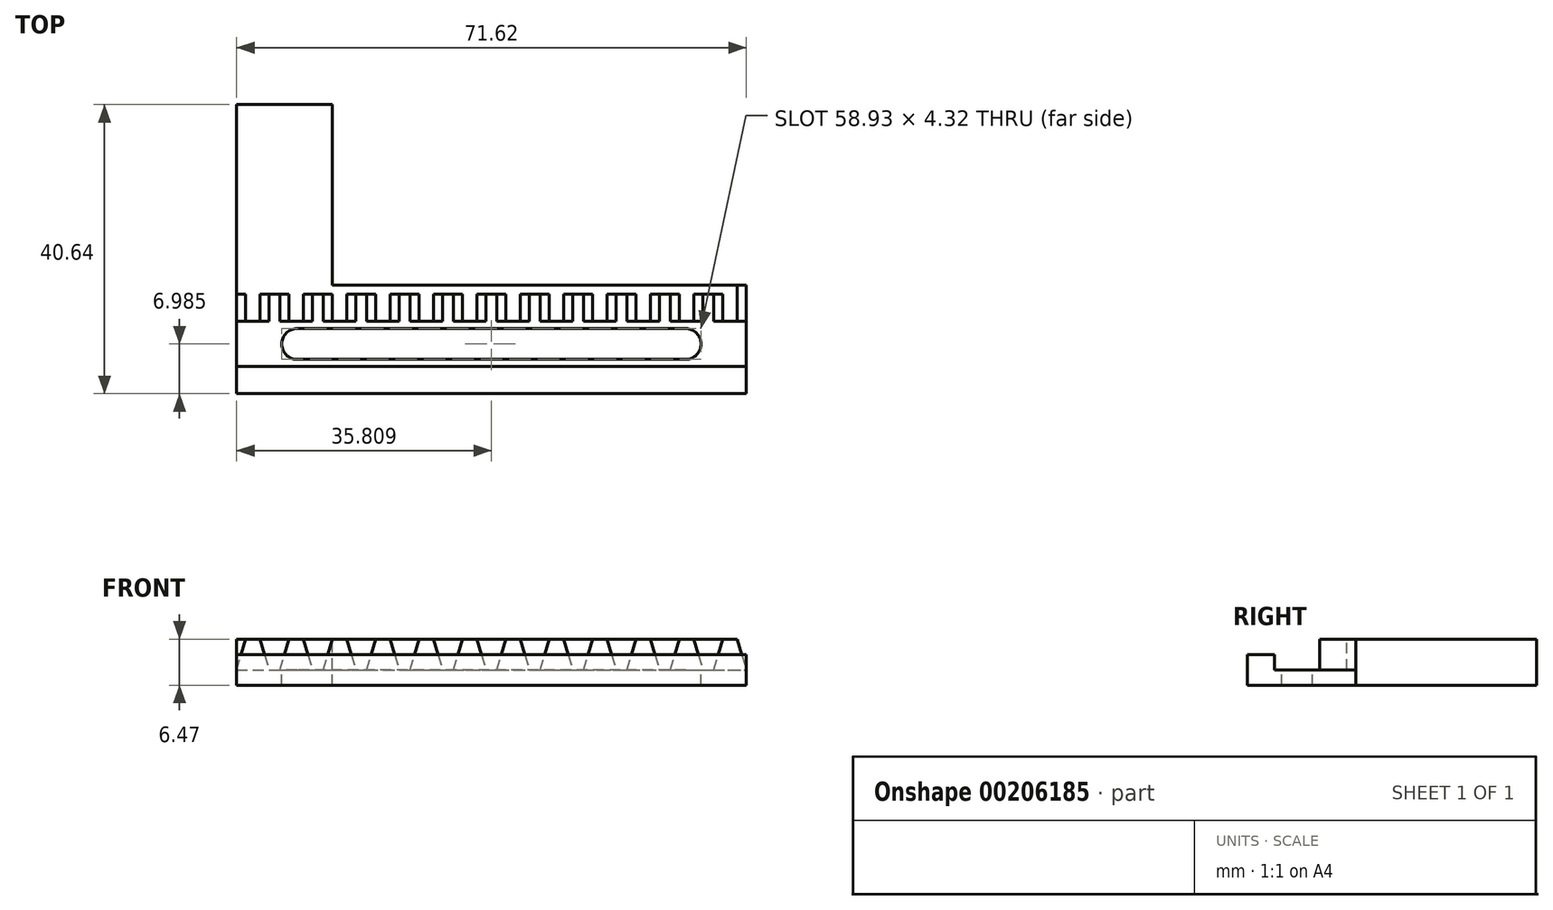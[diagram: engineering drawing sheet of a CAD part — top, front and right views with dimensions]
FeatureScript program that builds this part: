
annotation { "Feature Type Name" : "Feature", "Feature Type Description" : "" }
export const myFeature = defineFeature(function(context is Context, id is Id, definition is map)
    precondition{}
    {
        {
            var Q0;
            Q0=qCreatedBy(makeId("Front.planeOp"),FACE);
            var sketch = newSketch(context, id + "F0", { "sketchPlane" : qUnion([Q0])});
            skLineSegment(sketch, "E0.bottom", {"start": v(-38.44, 14.74) * mm, "end": v(33.18, 14.74) * mm});
            skLineSegment(sketch, "E0.top", {"start": v(-38.44, 16.9) * mm, "end": v(33.18, 16.9) * mm});
            skLineSegment(sketch, "E0.left", {"start": v(-38.44, 14.74) * mm, "end": v(-38.44, 16.9) * mm});
            skLineSegment(sketch, "E1", {"start": v(-38.44, 16.9) * mm, "end": v(-37.17, 21.21) * mm});
            skLineSegment(sketch, "E2", {"start": v(-37.17, 21.21) * mm, "end": v(-35.14, 21.21) * mm});
            skLineSegment(sketch, "E3", {"start": v(-35.14, 21.21) * mm, "end": v(-33.87, 16.9) * mm});
            skLineSegment(sketch, "E4", {"start": v(-38.44, 16.9) * mm, "end": v(-33.87, 16.9) * mm});
            skLineSegment(sketch, "E5", {"start": v(-36.16, 21.21) * mm, "end": v(-36.16, 16.9) * mm, "construction": true});
            skLineSegment(sketch, "E6", {"start": v(33.18, 14.74) * mm, "end": v(33.18, 16.9) * mm});
            skLineSegment(sketch, "E7.1.0.0", {"start": v(-29.05, 21.21) * mm, "end": v(-27.78, 16.9) * mm});
            skLineSegment(sketch, "E7.1.0.1", {"start": v(-32.35, 16.9) * mm, "end": v(-31.08, 21.21) * mm});
            skLineSegment(sketch, "E7.1.0.2", {"start": v(-31.08, 21.21) * mm, "end": v(-29.05, 21.21) * mm});
            skLineSegment(sketch, "E7.2.0.0", {"start": v(-22.95, 21.21) * mm, "end": v(-21.68, 16.9) * mm});
            skLineSegment(sketch, "E7.2.0.1", {"start": v(-26.25, 16.9) * mm, "end": v(-24.98, 21.21) * mm});
            skLineSegment(sketch, "E7.2.0.2", {"start": v(-24.98, 21.21) * mm, "end": v(-22.95, 21.21) * mm});
            skLineSegment(sketch, "E7.3.0.0", {"start": v(-16.85, 21.21) * mm, "end": v(-15.58, 16.9) * mm});
            skLineSegment(sketch, "E7.3.0.1", {"start": v(-20.16, 16.9) * mm, "end": v(-18.89, 21.21) * mm});
            skLineSegment(sketch, "E7.3.0.2", {"start": v(-18.89, 21.21) * mm, "end": v(-16.85, 21.21) * mm});
            skLineSegment(sketch, "E7.4.0.0", {"start": v(-10.76, 21.21) * mm, "end": v(-9.49, 16.9) * mm});
            skLineSegment(sketch, "E7.4.0.1", {"start": v(-14.06, 16.9) * mm, "end": v(-12.8, 21.21) * mm});
            skLineSegment(sketch, "E7.4.0.2", {"start": v(-12.8, 21.21) * mm, "end": v(-10.76, 21.21) * mm});
            skLineSegment(sketch, "E7.5.0.0", {"start": v(-4.66, 21.21) * mm, "end": v(-3.4, 16.9) * mm});
            skLineSegment(sketch, "E7.5.0.1", {"start": v(-7.96, 16.9) * mm, "end": v(-6.7, 21.21) * mm});
            skLineSegment(sketch, "E7.5.0.2", {"start": v(-6.7, 21.21) * mm, "end": v(-4.66, 21.21) * mm});
            skLineSegment(sketch, "E7.6.0.0", {"start": v(1.43, 21.21) * mm, "end": v(2.7, 16.9) * mm});
            skLineSegment(sketch, "E7.6.0.1", {"start": v(-1.87, 16.9) * mm, "end": v(-0.6, 21.21) * mm});
            skLineSegment(sketch, "E7.6.0.2", {"start": v(-0.6, 21.21) * mm, "end": v(1.43, 21.21) * mm});
            skLineSegment(sketch, "E7.7.0.0", {"start": v(7.53, 21.21) * mm, "end": v(8.8, 16.9) * mm});
            skLineSegment(sketch, "E7.7.0.1", {"start": v(4.23, 16.9) * mm, "end": v(5.5, 21.21) * mm});
            skLineSegment(sketch, "E7.7.0.2", {"start": v(5.5, 21.21) * mm, "end": v(7.53, 21.21) * mm});
            skLineSegment(sketch, "E7.8.0.0", {"start": v(13.63, 21.21) * mm, "end": v(14.9, 16.9) * mm});
            skLineSegment(sketch, "E7.8.0.1", {"start": v(10.32, 16.9) * mm, "end": v(11.6, 21.21) * mm});
            skLineSegment(sketch, "E7.8.0.2", {"start": v(11.6, 21.21) * mm, "end": v(13.63, 21.21) * mm});
            skLineSegment(sketch, "E7.9.0.0", {"start": v(19.72, 21.21) * mm, "end": v(21, 16.9) * mm});
            skLineSegment(sketch, "E7.9.0.1", {"start": v(16.42, 16.9) * mm, "end": v(17.69, 21.21) * mm});
            skLineSegment(sketch, "E7.9.0.2", {"start": v(17.69, 21.21) * mm, "end": v(19.72, 21.21) * mm});
            skLineSegment(sketch, "E7.10.0.0", {"start": v(25.82, 21.21) * mm, "end": v(27.09, 16.9) * mm});
            skLineSegment(sketch, "E7.10.0.1", {"start": v(22.52, 16.9) * mm, "end": v(23.79, 21.21) * mm});
            skLineSegment(sketch, "E7.10.0.2", {"start": v(23.79, 21.21) * mm, "end": v(25.82, 21.21) * mm});
            skLineSegment(sketch, "E7.11.0.0", {"start": v(31.91, 21.21) * mm, "end": v(33.18, 16.9) * mm});
            skLineSegment(sketch, "E7.11.0.1", {"start": v(28.61, 16.9) * mm, "end": v(29.88, 21.21) * mm});
            skLineSegment(sketch, "E7.11.0.2", {"start": v(29.88, 21.21) * mm, "end": v(31.91, 21.21) * mm});
            skLineSegment(sketch, "E7.direction1", {"start": v(-38.44, 16.9) * mm, "end": v(-32.35, 16.9) * mm, "construction": true});
            skPoint(sketch, "E8.centerSnap0", {"position": v(-38.44, 15.82) * mm});
            skSolve(sketch);
        }
        {
            var Q0;
            Q0=qSketchRegion(id+"F0",true);
            extrude(context, id + "F1", {"entities" : qUnion([Q0]), "depth" : 3.8 * mm});
        }
        {
            var Q0;
            Q0=qCreatedBy(makeId("Right.planeOp"),FACE);
            var Q1;
            Q1=makeQuery(id+"F1.opExtrude","CAP_VERTEX",VERTEX,{"disambiguationData":[OSD([sQuery(id+"F0.wireOp",EDGE,"E0.bottom"),sQuery(id+"F0.wireOp",EDGE,"E6")])],"isStart":false});
            cPlane(context, id + "F2", {"entities" : qUnion([Q0, Q1]), "cplaneType" : CPlaneType.PLANE_POINT, "offset" : 25.4 * mm, "width" : 152.4 * mm, "height" : 152.4 * mm});
        }
        {
            var Q0;
            Q0=qCreatedBy(id+"F2.planeOp",FACE);
            var sketch = newSketch(context, id + "F3", { "sketchPlane" : qUnion([Q0])});
            skLineSegment(sketch, "E9.0", {"start": v(-3.81, 14.74) * mm, "end": v(-3.81, 16.9) * mm});
            skLineSegment(sketch, "E10", {"start": v(-17.78, 16.9) * mm, "end": v(-13.97, 16.9) * mm});
            skLineSegment(sketch, "E11", {"start": v(-10.16, 16.9) * mm, "end": v(-10.16, 19.05) * mm});
            skLineSegment(sketch, "E12", {"start": v(-10.16, 19.05) * mm, "end": v(-13.97, 19.05) * mm});
            skLineSegment(sketch, "E13", {"start": v(-13.97, 19.05) * mm, "end": v(-13.97, 16.9) * mm});
            skLineSegment(sketch, "E14.trimOffspring", {"start": v(-10.16, 16.9) * mm, "end": v(-3.81, 16.9) * mm});
            skLineSegment(sketch, "E15", {"start": v(-3.81, 14.74) * mm, "end": v(-17.78, 14.74) * mm});
            skLineSegment(sketch, "E16", {"start": v(-17.78, 14.74) * mm, "end": v(-17.78, 16.9) * mm});
            skLineSegment(sketch, "E17", {"start": v(-13.97, 16.9) * mm, "end": v(-13.97, 14.74) * mm});
            skSolve(sketch);
        }
        {
            var Q0;
            {var subQ0=sQuery(id+"F3.wireOp",EDGE,"E9.0");Q0=makeQuery(id+"F3.imprint","IMPRINT",FACE,{"disambiguationData":[TD([[makeQuery(id+"F3.imprint","IMPRINT",EDGE,{"derivedFrom":subQ0}),1.0]])]});}
            var Q1;
            Q1=makeQuery(id+"F1.opExtrude","SWEPT_FACE",FACE,{"disambiguationData":[OSD([sQuery(id+"F0.wireOp",EDGE,"E0.left")])]});
            extrude(context, id + "F4", {"entities" : qUnion([Q0]), "operationType" : NewBodyOperationType.ADD, "endBound" : BoundingType.UP_TO_SURFACE, "oppositeDirection" : true, "endBoundEntityFace" : qUnion([Q1]), "depth" : 33.02 * mm});
        }
        {
            var Q0;
            Q0=makeQuery(id+"F1.opExtrude","CAP_FACE",FACE,{"disambiguationData":[OSD([sQuery(id+"F0.wireOp",EDGE,"E0.bottom"),sQuery(id+"F0.wireOp",EDGE,"E0.top"),sQuery(id+"F0.wireOp",EDGE,"E0.left"),sQuery(id+"F0.wireOp",EDGE,"E1"),sQuery(id+"F0.wireOp",EDGE,"E2"),sQuery(id+"F0.wireOp",EDGE,"E3"),sQuery(id+"F0.wireOp",EDGE,"E6"),sQuery(id+"F0.wireOp",EDGE,"E7.1.0.0"),sQuery(id+"F0.wireOp",EDGE,"E7.1.0.1"),sQuery(id+"F0.wireOp",EDGE,"E7.1.0.2"),sQuery(id+"F0.wireOp",EDGE,"E7.2.0.0"),sQuery(id+"F0.wireOp",EDGE,"E7.2.0.1"),sQuery(id+"F0.wireOp",EDGE,"E7.2.0.2"),sQuery(id+"F0.wireOp",EDGE,"E7.3.0.0"),sQuery(id+"F0.wireOp",EDGE,"E7.3.0.1"),sQuery(id+"F0.wireOp",EDGE,"E7.3.0.2"),sQuery(id+"F0.wireOp",EDGE,"E7.4.0.0"),sQuery(id+"F0.wireOp",EDGE,"E7.4.0.1"),sQuery(id+"F0.wireOp",EDGE,"E7.4.0.2"),sQuery(id+"F0.wireOp",EDGE,"E7.5.0.0"),sQuery(id+"F0.wireOp",EDGE,"E7.5.0.1"),sQuery(id+"F0.wireOp",EDGE,"E7.5.0.2"),sQuery(id+"F0.wireOp",EDGE,"E7.6.0.0"),sQuery(id+"F0.wireOp",EDGE,"E7.6.0.1"),sQuery(id+"F0.wireOp",EDGE,"E7.6.0.2"),sQuery(id+"F0.wireOp",EDGE,"E7.7.0.0"),sQuery(id+"F0.wireOp",EDGE,"E7.7.0.1"),sQuery(id+"F0.wireOp",EDGE,"E7.7.0.2"),sQuery(id+"F0.wireOp",EDGE,"E7.8.0.0"),sQuery(id+"F0.wireOp",EDGE,"E7.8.0.1"),sQuery(id+"F0.wireOp",EDGE,"E7.8.0.2"),sQuery(id+"F0.wireOp",EDGE,"E7.9.0.0"),sQuery(id+"F0.wireOp",EDGE,"E7.9.0.1"),sQuery(id+"F0.wireOp",EDGE,"E7.9.0.2"),sQuery(id+"F0.wireOp",EDGE,"E7.10.0.0"),sQuery(id+"F0.wireOp",EDGE,"E7.10.0.1"),sQuery(id+"F0.wireOp",EDGE,"E7.10.0.2"),sQuery(id+"F0.wireOp",EDGE,"E7.11.0.0"),sQuery(id+"F0.wireOp",EDGE,"E7.11.0.1"),sQuery(id+"F0.wireOp",EDGE,"E7.11.0.2")])],"isStart":true});
            var sketch = newSketch(context, id + "F5", { "sketchPlane" : qUnion([Q0])});
            skPoint(sketch, "E18.oppositeSnap0", {"position": v(23.97, 21.21) * mm});
            skLineSegment(sketch, "E18.bottom", {"start": v(38.44, 14.74) * mm, "end": v(-33.18, 14.74) * mm});
            skLineSegment(sketch, "E18.top", {"start": v(38.44, 21.21) * mm, "end": v(-33.18, 21.21) * mm});
            skLineSegment(sketch, "E18.left", {"start": v(38.44, 14.74) * mm, "end": v(38.44, 21.21) * mm});
            skLineSegment(sketch, "E18.right", {"start": v(-33.18, 14.74) * mm, "end": v(-33.18, 21.21) * mm});
            skLineSegment(sketch, "E19.0", {"start": v(-31.91, 21.21) * mm, "end": v(-33.18, 16.9) * mm});
            skLineSegment(sketch, "E20.0", {"start": v(38.44, 16.9) * mm, "end": v(37.17, 21.21) * mm});
            skSolve(sketch);
        }
        {
            var Q0;
            {var subQ1=sQuery(id+"F0.wireOp",EDGE,"E3");var subQ2=makeQuery(id+"F1.opExtrude","CAP_EDGE",EDGE,{"disambiguationData":[OSD([subQ1])],"isStart":true});Q0=makeQuery(id+"F5.imprint","IMPRINT",FACE,{"disambiguationData":[TD([[makeQuery(id+"F5.imprint","IMPRINT",EDGE,{"derivedFrom":subQ2}),-1.0]])]});}
            var Q1;
            {var subQ1=sQuery(id+"F0.wireOp",EDGE,"E7.1.0.0");var subQ2=makeQuery(id+"F1.opExtrude","CAP_EDGE",EDGE,{"disambiguationData":[OSD([subQ1])],"isStart":true});Q1=makeQuery(id+"F5.imprint","IMPRINT",FACE,{"disambiguationData":[TD([[makeQuery(id+"F5.imprint","IMPRINT",EDGE,{"derivedFrom":subQ2}),-1.0]])]});}
            var Q2;
            {var subQ1=sQuery(id+"F0.wireOp",EDGE,"E7.2.0.0");var subQ2=makeQuery(id+"F1.opExtrude","CAP_EDGE",EDGE,{"disambiguationData":[OSD([subQ1])],"isStart":true});Q2=makeQuery(id+"F5.imprint","IMPRINT",FACE,{"disambiguationData":[TD([[makeQuery(id+"F5.imprint","IMPRINT",EDGE,{"derivedFrom":subQ2}),-1.0]])]});}
            var Q3;
            {var subQ1=sQuery(id+"F0.wireOp",EDGE,"E7.3.0.0");var subQ2=makeQuery(id+"F1.opExtrude","CAP_EDGE",EDGE,{"disambiguationData":[OSD([subQ1])],"isStart":true});Q3=makeQuery(id+"F5.imprint","IMPRINT",FACE,{"disambiguationData":[TD([[makeQuery(id+"F5.imprint","IMPRINT",EDGE,{"derivedFrom":subQ2}),-1.0]])]});}
            var Q4;
            {var subQ1=sQuery(id+"F0.wireOp",EDGE,"E7.4.0.0");var subQ2=makeQuery(id+"F1.opExtrude","CAP_EDGE",EDGE,{"disambiguationData":[OSD([subQ1])],"isStart":true});Q4=makeQuery(id+"F5.imprint","IMPRINT",FACE,{"disambiguationData":[TD([[makeQuery(id+"F5.imprint","IMPRINT",EDGE,{"derivedFrom":subQ2}),-1.0]])]});}
            var Q5;
            {var subQ1=sQuery(id+"F0.wireOp",EDGE,"E7.5.0.0");var subQ2=makeQuery(id+"F1.opExtrude","CAP_EDGE",EDGE,{"disambiguationData":[OSD([subQ1])],"isStart":true});Q5=makeQuery(id+"F5.imprint","IMPRINT",FACE,{"disambiguationData":[TD([[makeQuery(id+"F5.imprint","IMPRINT",EDGE,{"derivedFrom":subQ2}),-1.0]])]});}
            var Q6;
            {var subQ1=sQuery(id+"F0.wireOp",EDGE,"E7.6.0.0");var subQ2=makeQuery(id+"F1.opExtrude","CAP_EDGE",EDGE,{"disambiguationData":[OSD([subQ1])],"isStart":true});Q6=makeQuery(id+"F5.imprint","IMPRINT",FACE,{"disambiguationData":[TD([[makeQuery(id+"F5.imprint","IMPRINT",EDGE,{"derivedFrom":subQ2}),-1.0]])]});}
            var Q7;
            {var subQ1=sQuery(id+"F0.wireOp",EDGE,"E7.7.0.0");var subQ2=makeQuery(id+"F1.opExtrude","CAP_EDGE",EDGE,{"disambiguationData":[OSD([subQ1])],"isStart":true});Q7=makeQuery(id+"F5.imprint","IMPRINT",FACE,{"disambiguationData":[TD([[makeQuery(id+"F5.imprint","IMPRINT",EDGE,{"derivedFrom":subQ2}),-1.0]])]});}
            var Q8;
            {var subQ1=sQuery(id+"F0.wireOp",EDGE,"E7.8.0.0");var subQ2=makeQuery(id+"F1.opExtrude","CAP_EDGE",EDGE,{"disambiguationData":[OSD([subQ1])],"isStart":true});Q8=makeQuery(id+"F5.imprint","IMPRINT",FACE,{"disambiguationData":[TD([[makeQuery(id+"F5.imprint","IMPRINT",EDGE,{"derivedFrom":subQ2}),-1.0]])]});}
            var Q9;
            {var subQ1=sQuery(id+"F0.wireOp",EDGE,"E7.9.0.0");var subQ2=makeQuery(id+"F1.opExtrude","CAP_EDGE",EDGE,{"disambiguationData":[OSD([subQ1])],"isStart":true});Q9=makeQuery(id+"F5.imprint","IMPRINT",FACE,{"disambiguationData":[TD([[makeQuery(id+"F5.imprint","IMPRINT",EDGE,{"derivedFrom":subQ2}),-1.0]])]});}
            var Q10;
            {var subQ1=sQuery(id+"F0.wireOp",EDGE,"E7.10.0.0");var subQ2=makeQuery(id+"F1.opExtrude","CAP_EDGE",EDGE,{"disambiguationData":[OSD([subQ1])],"isStart":true});Q10=makeQuery(id+"F5.imprint","IMPRINT",FACE,{"disambiguationData":[TD([[makeQuery(id+"F5.imprint","IMPRINT",EDGE,{"derivedFrom":subQ2}),-1.0]])]});}
            var Q11;
            {var subQ42=sQuery(id+"F5.wireOp",EDGE,"E18.bottom");Q11=makeQuery(id+"F5.imprint","IMPRINT",FACE,{"disambiguationData":[TD([[makeQuery(id+"F5.imprint","IMPRINT",EDGE,{"derivedFrom":subQ42}),-1.0]])]});}
            var Q12;
            {var subQ0=sQuery(id+"F5.wireOp",EDGE,"E20.0");Q12=makeQuery(id+"F5.imprint","IMPRINT",FACE,{"disambiguationData":[TD([[makeQuery(id+"F5.imprint","IMPRINT",EDGE,{"derivedFrom":subQ0}),-1.0]])]});}
            extrude(context, id + "F6", {"entities" : qUnion([Q0, Q1, Q2, Q3, Q4, Q5, Q6, Q7, Q8, Q9, Q10, Q11, Q12]), "operationType" : NewBodyOperationType.ADD, "depth" : 1.27 * mm});
        }
        {
            var Q0;
            Q0=makeQuery(id+"F6.opExtrude","CAP_FACE",FACE,{"disambiguationData":[OSD([sQuery(id+"F5.wireOp",EDGE,"E18.bottom"),sQuery(id+"F5.wireOp",EDGE,"E18.top"),sQuery(id+"F5.wireOp",EDGE,"E18.left"),sQuery(id+"F5.wireOp",EDGE,"E18.right")])],"isStart":false});
            var sketch = newSketch(context, id + "F7", { "sketchPlane" : qUnion([Q0])});
            skLineSegment(sketch, "E21.2", {"start": v(38.44, 14.74) * mm, "end": v(38.44, 21.21) * mm});
            skLineSegment(sketch, "E22", {"start": v(24.98, 14.74) * mm, "end": v(38.44, 14.74) * mm});
            skLineSegment(sketch, "E23", {"start": v(38.44, 21.21) * mm, "end": v(24.98, 21.21) * mm});
            skLineSegment(sketch, "E24", {"start": v(24.98, 14.74) * mm, "end": v(24.98, 21.21) * mm});
            skSolve(sketch);
        }
        {
            var Q0;
            Q0=qSketchRegion(id+"F7",true);
            extrude(context, id + "F8", {"entities" : qUnion([Q0]), "operationType" : NewBodyOperationType.ADD, "depth" : 25.4 * mm});
        }
        {
            var Q0;
            {var subQ0=sQuery(id+"F0.wireOp",EDGE,"E0.top");Q0=makeQuery(id+"F4.boolean.opBoolean","MERGE",FACE,{"derivedFrom":[makeQuery(id+"F1.opExtrude","SWEPT_FACE",FACE,{"disambiguationData":[OSD([subQ0]),TDD([makeQuery(id+"F0.imprint","IMPRINT",EDGE,{"disambiguationData":[TD([[makeQuery(id+"F0.imprint","INTERSECT",VERTEX,{"derivedFrom":[subQ0,sQuery(id+"F0.wireOp",EDGE,"E7.1.0.1")]}),1.0]])],"derivedFrom":subQ0})])]}),makeQuery(id+"F1.opExtrude","SWEPT_FACE",FACE,{"disambiguationData":[OSD([subQ0]),TDD([makeQuery(id+"F0.imprint","IMPRINT",EDGE,{"disambiguationData":[TD([[makeQuery(id+"F0.imprint","INTERSECT",VERTEX,{"derivedFrom":[subQ0,sQuery(id+"F0.wireOp",EDGE,"E7.1.0.0")]}),-1.0]])],"derivedFrom":subQ0})])]}),makeQuery(id+"F1.opExtrude","SWEPT_FACE",FACE,{"disambiguationData":[OSD([subQ0]),TDD([makeQuery(id+"F0.imprint","IMPRINT",EDGE,{"disambiguationData":[TD([[makeQuery(id+"F0.imprint","INTERSECT",VERTEX,{"derivedFrom":[subQ0,sQuery(id+"F0.wireOp",EDGE,"E7.2.0.0")]}),-1.0]])],"derivedFrom":subQ0})])]}),makeQuery(id+"F1.opExtrude","SWEPT_FACE",FACE,{"disambiguationData":[OSD([subQ0]),TDD([makeQuery(id+"F0.imprint","IMPRINT",EDGE,{"disambiguationData":[TD([[makeQuery(id+"F0.imprint","INTERSECT",VERTEX,{"derivedFrom":[subQ0,sQuery(id+"F0.wireOp",EDGE,"E7.3.0.0")]}),-1.0]])],"derivedFrom":subQ0})])]}),makeQuery(id+"F1.opExtrude","SWEPT_FACE",FACE,{"disambiguationData":[OSD([subQ0]),TDD([makeQuery(id+"F0.imprint","IMPRINT",EDGE,{"disambiguationData":[TD([[makeQuery(id+"F0.imprint","INTERSECT",VERTEX,{"derivedFrom":[subQ0,sQuery(id+"F0.wireOp",EDGE,"E7.4.0.0")]}),-1.0]])],"derivedFrom":subQ0})])]}),makeQuery(id+"F1.opExtrude","SWEPT_FACE",FACE,{"disambiguationData":[OSD([subQ0]),TDD([makeQuery(id+"F0.imprint","IMPRINT",EDGE,{"disambiguationData":[TD([[makeQuery(id+"F0.imprint","INTERSECT",VERTEX,{"derivedFrom":[subQ0,sQuery(id+"F0.wireOp",EDGE,"E7.5.0.0")]}),-1.0]])],"derivedFrom":subQ0})])]}),makeQuery(id+"F1.opExtrude","SWEPT_FACE",FACE,{"disambiguationData":[OSD([subQ0]),TDD([makeQuery(id+"F0.imprint","IMPRINT",EDGE,{"disambiguationData":[TD([[makeQuery(id+"F0.imprint","INTERSECT",VERTEX,{"derivedFrom":[subQ0,sQuery(id+"F0.wireOp",EDGE,"E7.6.0.0")]}),-1.0]])],"derivedFrom":subQ0})])]}),makeQuery(id+"F1.opExtrude","SWEPT_FACE",FACE,{"disambiguationData":[OSD([subQ0]),TDD([makeQuery(id+"F0.imprint","IMPRINT",EDGE,{"disambiguationData":[TD([[makeQuery(id+"F0.imprint","INTERSECT",VERTEX,{"derivedFrom":[subQ0,sQuery(id+"F0.wireOp",EDGE,"E7.7.0.0")]}),-1.0]])],"derivedFrom":subQ0})])]}),makeQuery(id+"F1.opExtrude","SWEPT_FACE",FACE,{"disambiguationData":[OSD([subQ0]),TDD([makeQuery(id+"F0.imprint","IMPRINT",EDGE,{"disambiguationData":[TD([[makeQuery(id+"F0.imprint","INTERSECT",VERTEX,{"derivedFrom":[subQ0,sQuery(id+"F0.wireOp",EDGE,"E7.8.0.0")]}),-1.0]])],"derivedFrom":subQ0})])]}),makeQuery(id+"F1.opExtrude","SWEPT_FACE",FACE,{"disambiguationData":[OSD([subQ0]),TDD([makeQuery(id+"F0.imprint","IMPRINT",EDGE,{"disambiguationData":[TD([[makeQuery(id+"F0.imprint","INTERSECT",VERTEX,{"derivedFrom":[subQ0,sQuery(id+"F0.wireOp",EDGE,"E7.9.0.0")]}),-1.0]])],"derivedFrom":subQ0})])]}),makeQuery(id+"F1.opExtrude","SWEPT_FACE",FACE,{"disambiguationData":[OSD([subQ0]),TDD([makeQuery(id+"F0.imprint","IMPRINT",EDGE,{"disambiguationData":[TD([[makeQuery(id+"F0.imprint","INTERSECT",VERTEX,{"derivedFrom":[subQ0,sQuery(id+"F0.wireOp",EDGE,"E7.10.0.0")]}),-1.0]])],"derivedFrom":subQ0})])]}),makeQuery(id+"F4.opExtrude","SWEPT_FACE",FACE,{"disambiguationData":[OSD([sQuery(id+"F3.wireOp",EDGE,"E14.trimOffspring")])]})]});}
            var sketch = newSketch(context, id + "F9", { "sketchPlane" : qUnion([Q0])});
            skLineSegment(sketch, "E25.bottom", {"start": v(24.67, -9.14) * mm, "end": v(-29.94, -9.14) * mm});
            skLineSegment(sketch, "E25.top", {"start": v(24.67, -4.83) * mm, "end": v(-29.94, -4.83) * mm});
            skLineSegment(sketch, "E25.left", {"start": v(24.67, -9.14) * mm, "end": v(24.67, -4.83) * mm});
            skLineSegment(sketch, "E25.right", {"start": v(-29.94, -9.14) * mm, "end": v(-29.94, -4.83) * mm});
            skArc(sketch, "E26", {"start": v(24.67, -9.14) * mm, "mid": v(26.83, -6.99) * mm, "end": v(24.67, -4.83) * mm});
            skArc(sketch, "E27", {"start": v(-29.94, -4.83) * mm, "mid": v(-32.1, -6.99) * mm, "end": v(-29.94, -9.14) * mm});
            skSolve(sketch);
        }
        {
            var Q0;
            Q0=qSketchRegion(id+"F9",true);
            extrude(context, id + "F10", {"entities" : qUnion([Q0]), "operationType" : NewBodyOperationType.REMOVE, "oppositeDirection" : true, "depth" : 25.4 * mm});
        }
    });
